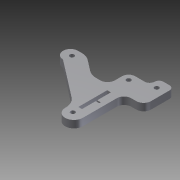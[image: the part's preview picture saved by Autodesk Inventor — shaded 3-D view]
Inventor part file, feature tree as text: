
AUTODESK INVENTOR PART (.ipt)
format: ipt  version: 2012 (Build 160160000, 160)  size: 173,568 bytes
history: native  units: mm
features: sketch x2, extrude x1, hole x1
ambient origin geometry x8: Origin, YZ Plane, XZ Plane, XY Plane, X Axis, Y Axis, Z Axis, Center Point
bodies: Solid1 (feature_tree)
feature tree (4):
  extrude  "Extrusion1"  Depth=48.0mm
  hole  "Hole1"  [1 undecoded]
  sketch  "Sketch1"  dims[d14=5.0mm d15=0.0mm]
  sketch  "Sketch2"  dims[d16=1.25mm d17=2.5mm d18=19.8mm d19=5.0mm d20=9.4mm d21=2.5mm d22=1.0mm d23=5.0mm d24=5.0mm d25=10.0mm d26=10.0mm d27=5.0mm d28=3.0mm d29=3.0mm d30=3.0mm d31=6.0mm d32=4.0mm d33=2.0mm d34=90.0deg d35=8.0mm d36=20.594885mm d37=48.0mm d39=10.0mm d40=60.0mm d41=6.75mm d42=0.75mm d43=5.25mm d44=5.0mm d45=33.2mm d46=1.25mm d47=2.5mm d48=19.8mm d49=5.0mm d50=9.4mm d51=2.5mm d52=1.0mm d53=5.0mm d54=5.0mm d55=10.0mm d56=10.0mm d57=5.0mm d58=3.0mm d59=3.0mm d62=60.0mm d63=6.75mm d64=0.75mm d65=5.25mm d66=5.0mm]
note: 1 required parameter value undecoded (feature->parameter linkage not recoverable at this tier; creation-order binding heuristic only, values carry confidence <= 0.55)
